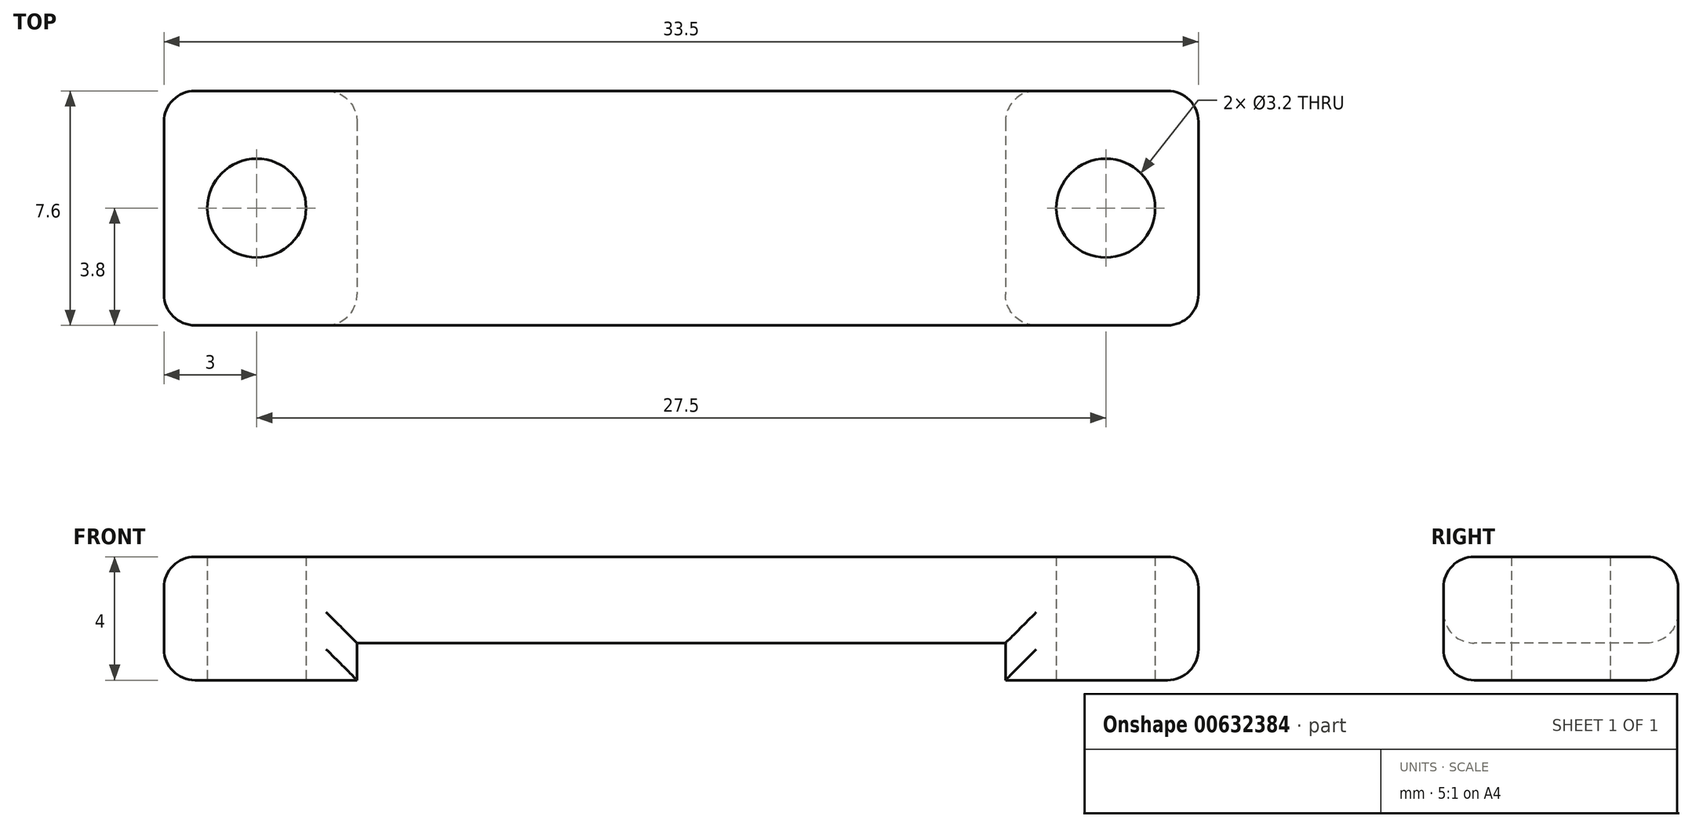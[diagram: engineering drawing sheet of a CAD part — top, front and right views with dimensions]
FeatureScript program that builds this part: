
annotation { "Feature Type Name" : "Feature", "Feature Type Description" : "" }
export const myFeature = defineFeature(function(context is Context, id is Id, definition is map)
    precondition{}
    {
        {
            var Q0;
            Q0=qCreatedBy(makeId("Top.planeOp"),FACE);
            var sketch = newSketch(context, id + "F0", { "sketchPlane" : qUnion([Q0])});
            skLineSegment(sketch, "E0.bottom", {"start": v(-10.5, 3.8) * mm, "end": v(10.5, 3.8) * mm});
            skLineSegment(sketch, "E0.top", {"start": v(-10.5, -3.8) * mm, "end": v(10.5, -3.8) * mm});
            skLineSegment(sketch, "E0.left", {"start": v(-10.5, 3.8) * mm, "end": v(-10.5, -3.8) * mm});
            skLineSegment(sketch, "E0.right", {"start": v(10.5, 3.8) * mm, "end": v(10.5, -3.8) * mm});
            skLineSegment(sketch, "E1.bottom", {"start": v(-10.75, 3.8) * mm, "end": v(10.75, 3.8) * mm});
            skLineSegment(sketch, "E1.top", {"start": v(-10.75, -3.8) * mm, "end": v(10.75, -3.8) * mm});
            skLineSegment(sketch, "E1.left", {"start": v(-10.75, 3.8) * mm, "end": v(-10.75, -3.8) * mm});
            skLineSegment(sketch, "E1.right", {"start": v(10.75, 3.8) * mm, "end": v(10.75, -3.8) * mm});
            skLineSegment(sketch, "E2.bottom", {"start": v(-16.75, 3.8) * mm, "end": v(16.75, 3.8) * mm});
            skLineSegment(sketch, "E2.top", {"start": v(-16.75, -3.8) * mm, "end": v(16.75, -3.8) * mm});
            skLineSegment(sketch, "E2.left", {"start": v(-16.75, 3.8) * mm, "end": v(-16.75, -3.8) * mm});
            skLineSegment(sketch, "E2.right", {"start": v(16.75, 3.8) * mm, "end": v(16.75, -3.8) * mm});
            skCircle(sketch, "E3", {"center": v(-13.75, 0) * mm, "radius": 1.6 * mm});
            skCircle(sketch, "E4", {"center": v(13.75, 0) * mm, "radius": 1.6 * mm});
            skLineSegment(sketch, "E5", {"start": v(10.75, -3.8) * mm, "end": v(16.75, 3.8) * mm, "construction": true});
            skSolve(sketch);
        }
        {
            var Q0;
            {var subQ2=sQuery(id+"F0.wireOp",EDGE,"E1.left");Q0=makeQuery(id+"F0.imprint","IMPRINT",FACE,{"disambiguationData":[TD([[makeQuery(id+"F0.imprint","IMPRINT",EDGE,{"derivedFrom":subQ2}),-1.0]])]});}
            var Q1;
            {var subQ2=sQuery(id+"F0.wireOp",EDGE,"E1.right");Q1=makeQuery(id+"F0.imprint","IMPRINT",FACE,{"disambiguationData":[TD([[makeQuery(id+"F0.imprint","IMPRINT",EDGE,{"derivedFrom":subQ2}),1.0]])]});}
            var Q2;
            {var subQ0=sQuery(id+"F0.wireOp",EDGE,"E0.left");Q2=makeQuery(id+"F0.imprint","IMPRINT",FACE,{"disambiguationData":[TD([[makeQuery(id+"F0.imprint","IMPRINT",EDGE,{"derivedFrom":subQ0}),-1.0]])]});}
            var Q3;
            {var subQ0=sQuery(id+"F0.wireOp",EDGE,"E0.left");Q3=makeQuery(id+"F0.imprint","IMPRINT",FACE,{"disambiguationData":[TD([[makeQuery(id+"F0.imprint","IMPRINT",EDGE,{"derivedFrom":subQ0}),1.0]])]});}
            var Q4;
            {var subQ0=sQuery(id+"F0.wireOp",EDGE,"E0.right");Q4=makeQuery(id+"F0.imprint","IMPRINT",FACE,{"disambiguationData":[TD([[makeQuery(id+"F0.imprint","IMPRINT",EDGE,{"derivedFrom":subQ0}),1.0]])]});}
            extrude(context, id + "F1", {"entities" : qUnion([Q0, Q1, Q2, Q3, Q4]), "depth" : 4 * mm, "offsetDistance" : 25 * mm});
        }
        {
            var Q0;
            {var subQ0=sQuery(id+"F0.wireOp",EDGE,"E0.left");Q0=makeQuery(id+"F0.imprint","IMPRINT",FACE,{"disambiguationData":[TD([[makeQuery(id+"F0.imprint","IMPRINT",EDGE,{"derivedFrom":subQ0}),1.0]])]});}
            extrude(context, id + "F2", {"entities" : qUnion([Q0]), "operationType" : NewBodyOperationType.REMOVE, "depth" : 1.2 * mm, "offsetDistance" : 25 * mm});
        }
        {
            var Q0;
            Q0=makeQuery(id+"F1.opExtrude","SWEPT_FACE",FACE,{"disambiguationData":[OSD([sQuery(id+"F0.wireOp",EDGE,"E2.top")])]});
            var Q1;
            Q1=makeQuery(id+"F1.opExtrude","SWEPT_FACE",FACE,{"disambiguationData":[OSD([sQuery(id+"F0.wireOp",EDGE,"E2.bottom")])]});
            var Q2;
            Q2=makeQuery(id+"F1.opExtrude","SWEPT_FACE",FACE,{"disambiguationData":[OSD([sQuery(id+"F0.wireOp",EDGE,"E2.right")])]});
            var Q3;
            Q3=makeQuery(id+"F1.opExtrude","SWEPT_FACE",FACE,{"disambiguationData":[OSD([sQuery(id+"F0.wireOp",EDGE,"E2.left")])]});
            fillet(context, id + "F3", {"entities" : qUnion([Q0, Q1, Q2, Q3]), "radius" : 1 * mm, "tangentPropagation" : true, "allowEdgeOverflow" : false});
        }
    });
